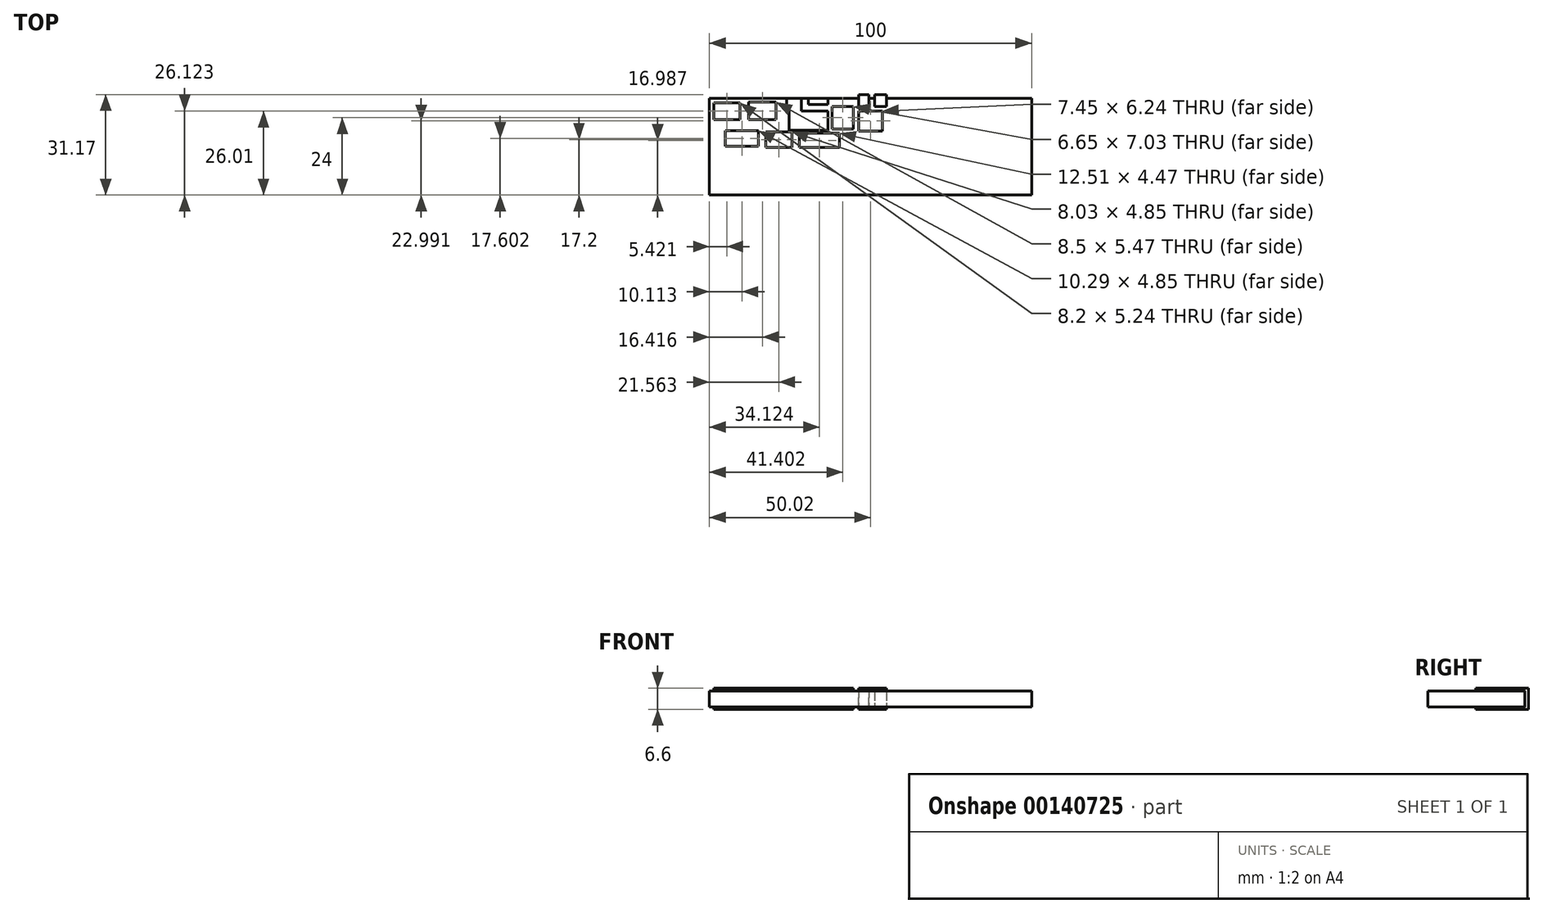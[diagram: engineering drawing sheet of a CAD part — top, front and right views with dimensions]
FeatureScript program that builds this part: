
annotation { "Feature Type Name" : "Feature", "Feature Type Description" : "" }
export const myFeature = defineFeature(function(context is Context, id is Id, definition is map)
    precondition{}
    {
        {
            var Q0;
            Q0=qCreatedBy(makeId("Top.planeOp"),FACE);
            var sketch = newSketch(context, id + "F0", { "sketchPlane" : qUnion([Q0])});
            skLineSegment(sketch, "E0.bottom", {"start": v(-61.69, 6.61) * mm, "end": v(38.31, 6.61) * mm});
            skLineSegment(sketch, "E0.top", {"start": v(-61.69, -23.39) * mm, "end": v(38.31, -23.39) * mm});
            skLineSegment(sketch, "E0.left", {"start": v(-61.69, 6.61) * mm, "end": v(-61.69, -23.39) * mm});
            skLineSegment(sketch, "E0.right", {"start": v(38.31, 6.61) * mm, "end": v(38.31, -23.39) * mm});
            skSolve(sketch);
        }
        {
            var Q0;
            Q0=makeQuery(id+"F0.imprint","IMPRINT",FACE,{"disambiguationData":[TD([[makeQuery(id+"F0.imprint","IMPRINT",EDGE,{"derivedFrom":sQuery(id+"F0.wireOp",EDGE,"E0.bottom")}),-1.0]])]});
            extrude(context, id + "F1", {"entities" : qUnion([Q0]), "depth" : 5 * mm});
        }
        {
            var Q0;
            Q0=makeQuery(id+"F1.opExtrude","CAP_FACE",FACE,{"disambiguationData":[OSD([sQuery(id+"F0.wireOp",EDGE,"E0.bottom"),sQuery(id+"F0.wireOp",EDGE,"E0.top"),sQuery(id+"F0.wireOp",EDGE,"E0.left"),sQuery(id+"F0.wireOp",EDGE,"E0.right")])],"isStart":false});
            var sketch = newSketch(context, id + "F2", { "sketchPlane" : qUnion([Q0])});
            skLineSegment(sketch, "E1.bottom", {"start": v(-60.37, 5.24) * mm, "end": v(-52.17, 5.24) * mm});
            skLineSegment(sketch, "E1.top", {"start": v(-60.37, 0) * mm, "end": v(-52.17, 0) * mm});
            skLineSegment(sketch, "E1.left", {"start": v(-60.37, 5.24) * mm, "end": v(-60.37, 0) * mm});
            skLineSegment(sketch, "E1.right", {"start": v(-52.17, 5.24) * mm, "end": v(-52.17, 0) * mm});
            skLineSegment(sketch, "E2.bottom", {"start": v(-56.72, -3.36) * mm, "end": v(-46.43, -3.36) * mm});
            skLineSegment(sketch, "E2.top", {"start": v(-56.72, -8.21) * mm, "end": v(-46.43, -8.21) * mm});
            skLineSegment(sketch, "E2.left", {"start": v(-56.72, -3.36) * mm, "end": v(-56.72, -8.21) * mm});
            skLineSegment(sketch, "E2.right", {"start": v(-46.43, -3.36) * mm, "end": v(-46.43, -8.21) * mm});
            skLineSegment(sketch, "E3.bottom", {"start": v(-49.52, 5.47) * mm, "end": v(-41.02, 5.47) * mm});
            skLineSegment(sketch, "E3.top", {"start": v(-49.52, 0) * mm, "end": v(-41.02, 0) * mm});
            skLineSegment(sketch, "E3.left", {"start": v(-49.52, 5.47) * mm, "end": v(-49.52, 0) * mm});
            skLineSegment(sketch, "E3.right", {"start": v(-41.02, 5.47) * mm, "end": v(-41.02, 0) * mm});
            skLineSegment(sketch, "E4.bottom", {"start": v(-36.99, 2.72) * mm, "end": v(-24.95, 2.72) * mm});
            skLineSegment(sketch, "E4.top", {"start": v(-36.99, -3.26) * mm, "end": v(-24.95, -3.26) * mm});
            skLineSegment(sketch, "E4.left", {"start": v(-36.99, 2.72) * mm, "end": v(-36.99, -3.26) * mm});
            skLineSegment(sketch, "E4.right", {"start": v(-24.95, 2.72) * mm, "end": v(-24.95, -3.26) * mm});
            skLineSegment(sketch, "E5.bottom", {"start": v(-44.14, -3.76) * mm, "end": v(-36.11, -3.76) * mm});
            skLineSegment(sketch, "E5.top", {"start": v(-44.14, -8.62) * mm, "end": v(-36.11, -8.62) * mm});
            skLineSegment(sketch, "E5.left", {"start": v(-44.14, -3.76) * mm, "end": v(-44.14, -8.62) * mm});
            skLineSegment(sketch, "E5.right", {"start": v(-36.11, -3.76) * mm, "end": v(-36.11, -8.62) * mm});
            skLineSegment(sketch, "E6.bottom", {"start": v(-33.82, -4.17) * mm, "end": v(-21.31, -4.17) * mm});
            skLineSegment(sketch, "E6.top", {"start": v(-33.82, -8.64) * mm, "end": v(-21.31, -8.64) * mm});
            skLineSegment(sketch, "E6.left", {"start": v(-33.82, -4.17) * mm, "end": v(-33.82, -8.64) * mm});
            skLineSegment(sketch, "E6.right", {"start": v(-21.31, -4.17) * mm, "end": v(-21.31, -8.64) * mm});
            skLineSegment(sketch, "E7.bottom", {"start": v(-23.61, 4.12) * mm, "end": v(-16.96, 4.12) * mm});
            skLineSegment(sketch, "E7.top", {"start": v(-23.61, -2.9) * mm, "end": v(-16.96, -2.9) * mm});
            skLineSegment(sketch, "E7.left", {"start": v(-23.61, 4.12) * mm, "end": v(-23.61, -2.9) * mm});
            skLineSegment(sketch, "E7.right", {"start": v(-16.96, 4.12) * mm, "end": v(-16.96, -2.9) * mm});
            skLineSegment(sketch, "E8.bottom", {"start": v(-37.7, 6.61) * mm, "end": v(-33.17, 6.61) * mm});
            skLineSegment(sketch, "E8.top", {"start": v(-37.7, 2.72) * mm, "end": v(-33.17, 2.72) * mm});
            skLineSegment(sketch, "E8.left", {"start": v(-37.7, 6.61) * mm, "end": v(-37.7, 2.72) * mm});
            skLineSegment(sketch, "E8.right", {"start": v(-33.17, 6.61) * mm, "end": v(-33.17, 2.72) * mm});
            skPoint(sketch, "E9.oppositeSnap0", {"position": v(-33.17, 4.67) * mm});
            skLineSegment(sketch, "E9.bottom", {"start": v(-31.04, 6.61) * mm, "end": v(-24.95, 6.61) * mm});
            skLineSegment(sketch, "E9.top", {"start": v(-31.04, 4.67) * mm, "end": v(-24.95, 4.67) * mm});
            skLineSegment(sketch, "E9.left", {"start": v(-31.04, 6.61) * mm, "end": v(-31.04, 4.67) * mm});
            skLineSegment(sketch, "E9.right", {"start": v(-24.95, 6.61) * mm, "end": v(-24.95, 4.67) * mm});
            skLineSegment(sketch, "E10.bottom", {"start": v(-15.4, 2.72) * mm, "end": v(-7.95, 2.72) * mm});
            skLineSegment(sketch, "E10.top", {"start": v(-15.4, -3.52) * mm, "end": v(-7.95, -3.52) * mm});
            skLineSegment(sketch, "E10.left", {"start": v(-15.4, 2.72) * mm, "end": v(-15.4, -3.52) * mm});
            skLineSegment(sketch, "E10.right", {"start": v(-7.95, 2.72) * mm, "end": v(-7.95, -3.52) * mm});
            skLineSegment(sketch, "E11.bottom", {"start": v(-12.2, 4.12) * mm, "end": v(-15.4, 4.12) * mm});
            skLineSegment(sketch, "E11.top", {"start": v(-12.2, 7.78) * mm, "end": v(-15.4, 7.78) * mm});
            skLineSegment(sketch, "E11.left", {"start": v(-12.2, 4.12) * mm, "end": v(-12.2, 7.78) * mm});
            skLineSegment(sketch, "E11.right", {"start": v(-15.4, 4.12) * mm, "end": v(-15.4, 7.78) * mm});
            skLineSegment(sketch, "E12.bottom", {"start": v(-10.43, 7.78) * mm, "end": v(-6.7, 7.78) * mm});
            skLineSegment(sketch, "E12.top", {"start": v(-10.43, 4.12) * mm, "end": v(-6.7, 4.12) * mm});
            skLineSegment(sketch, "E12.left", {"start": v(-10.43, 7.78) * mm, "end": v(-10.43, 4.12) * mm});
            skLineSegment(sketch, "E12.right", {"start": v(-6.7, 7.78) * mm, "end": v(-6.7, 4.12) * mm});
            skSolve(sketch);
        }
        {
            var Q0;
            Q0 = qSketchRegion(id + "F2", true);
            extrude(context, id + "F3", {"entities" : qUnion([Q0]), "operationType" : NewBodyOperationType.ADD, "depth" : 0.9 * mm, "hasSecondDirection" : true, "secondDirectionOppositeDirection" : true, "secondDirectionDepth" : 5.7 * mm});
        }
    });
